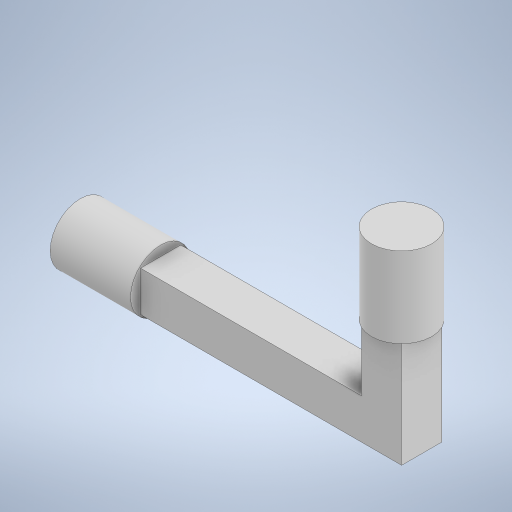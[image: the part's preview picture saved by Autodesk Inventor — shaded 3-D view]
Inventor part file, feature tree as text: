
AUTODESK INVENTOR PART (.ipt)
format: ipt  version: 2024.3 (Build 283343000, 343)  size: 247,808 bytes
history: native  units: mm
features: extrude x3, sketch x3, other x1
ambient origin geometry x8: Origin, YZ Plane, XZ Plane, XY Plane, X Axis, Y Axis, Z Axis, Center Point
bodies: Body1 (feature_tree)
feature tree (7):
  other  "ソリッド1"
  extrude  "押し出し1"  Depth=10.0mm
  extrude  "押し出し2"  Depth=10.0mm
  extrude  "押し出し3"  Depth=46.5mm
  sketch  "スケッチ1"
  sketch  "スケッチ2"
  sketch  "スケッチ3"
